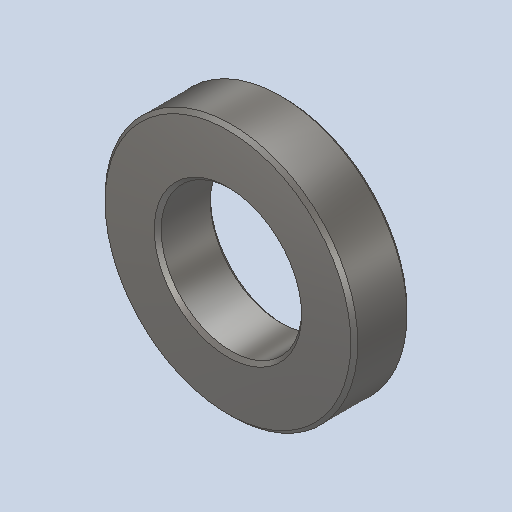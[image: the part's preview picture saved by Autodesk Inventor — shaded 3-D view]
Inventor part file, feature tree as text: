
AUTODESK INVENTOR PART (.ipt)
format: ipt  version: 2022.3 (Build 263350000, 350)  size: 129,536 bytes
history: native  units: in
note: dims shown in document units (in); Inventor stores cm internally (conversion verified against a paired STEP export)
features: extrude x1, chamfer x1, sketch x1
ambient origin geometry x8: Origin, YZ Plane, XZ Plane, XY Plane, X Axis, Y Axis, Z Axis, Center Point
bodies: Solid1 (feature_tree)
feature tree (3):
  extrude  "Extrusion1"  Depth=0.5in
  chamfer  "Chamfer1"  Distance=0.5in
  sketch  "Sketch1"  dims[d0=2.25in d1=1.25in d2=0.5in d3=0.0in d4=0.0312in d5=0.125in d6=45.0deg]
